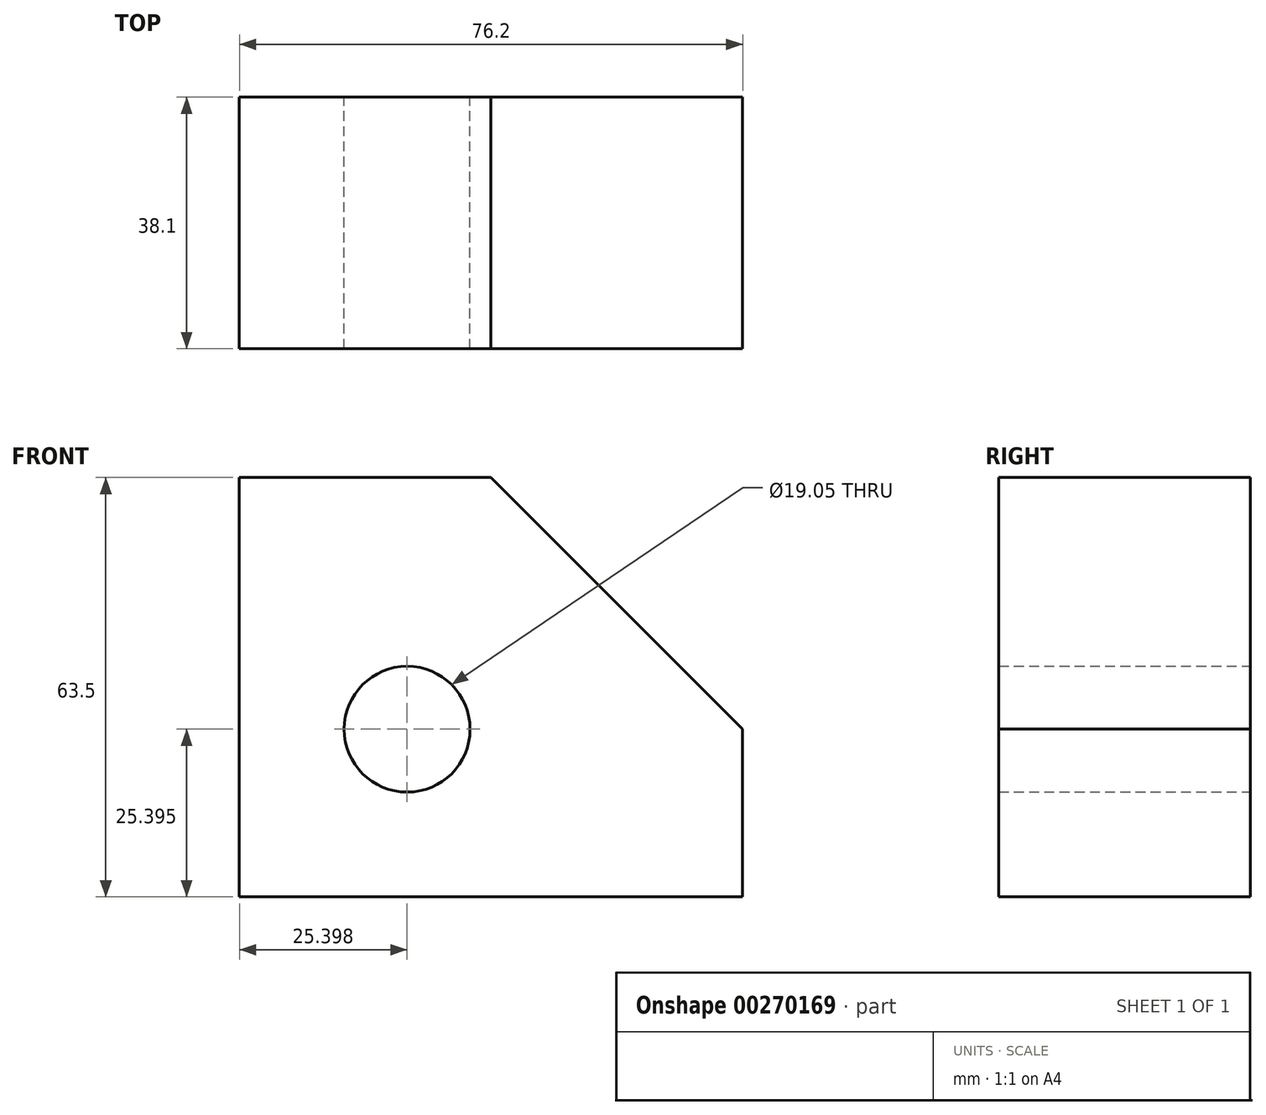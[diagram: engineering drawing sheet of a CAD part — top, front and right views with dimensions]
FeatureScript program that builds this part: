
annotation { "Feature Type Name" : "Feature", "Feature Type Description" : "" }
export const myFeature = defineFeature(function(context is Context, id is Id, definition is map)
    precondition{}
    {
        {
            var Q0;
            Q0=qCreatedBy(makeId("Front.planeOp"),FACE);
            var sketch = newSketch(context, id + "F0", { "sketchPlane" : qUnion([Q0])});
            skLineSegment(sketch, "E0", {"start": v(-33.27, -43.81) * mm, "end": v(42.93, -43.81) * mm});
            skLineSegment(sketch, "E1", {"start": v(42.93, -43.81) * mm, "end": v(42.93, -18.41) * mm});
            skLineSegment(sketch, "E2", {"start": v(42.93, -18.41) * mm, "end": v(4.83, 19.69) * mm});
            skLineSegment(sketch, "E3", {"start": v(4.83, 19.69) * mm, "end": v(-33.27, 19.69) * mm});
            skLineSegment(sketch, "E4", {"start": v(-33.27, 19.69) * mm, "end": v(-33.27, -43.81) * mm});
            skCircle(sketch, "E5", {"center": v(-7.87, -18.41) * mm, "radius": 9.53 * mm});
            skSolve(sketch);
        }
        {
            var Q0;
            Q0=makeQuery(id+"F0.imprint","IMPRINT",FACE,{"disambiguationData":[TD([[makeQuery(id+"F0.imprint","IMPRINT",EDGE,{"derivedFrom":sQuery(id+"F0.wireOp",EDGE,"E0")}),1.0]])]});
            extrude(context, id + "F1", {"entities" : qUnion([Q0]), "depth" : 38.1 * mm, "symmetric" : true});
        }
    });
